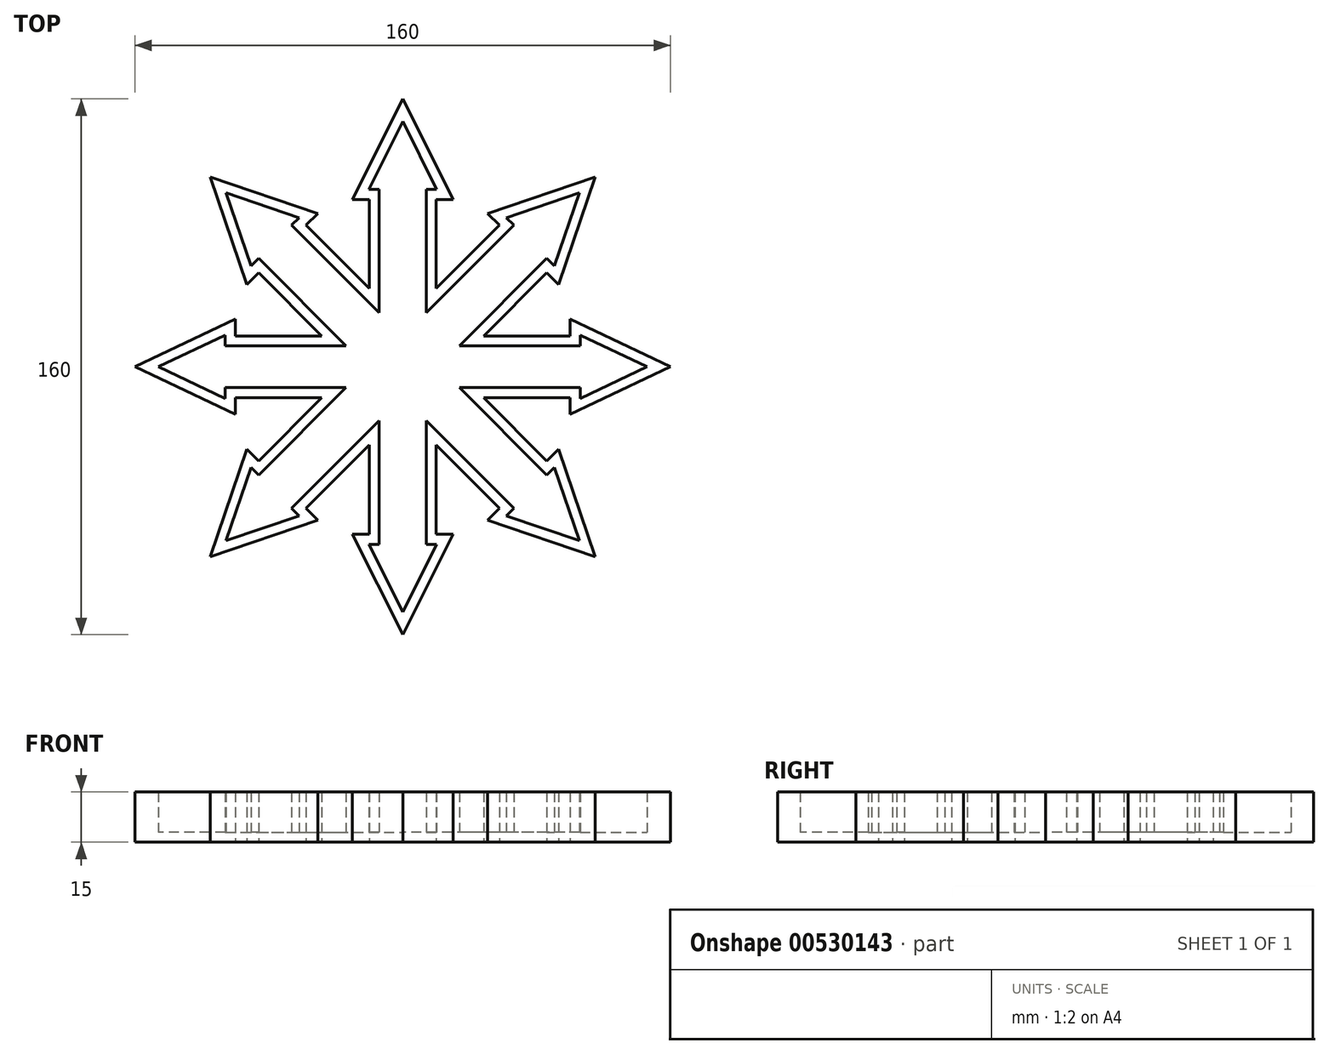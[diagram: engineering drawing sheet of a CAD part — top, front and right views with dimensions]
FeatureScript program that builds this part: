
annotation { "Feature Type Name" : "Feature", "Feature Type Description" : "" }
export const myFeature = defineFeature(function(context is Context, id is Id, definition is map)
    precondition{}
    {
        {
            var Q0;
            Q0=qCreatedBy(makeId("Top.planeOp"),FACE);
            var sketch = newSketch(context, id + "F0", { "sketchPlane" : qUnion([Q0])});
            skPoint(sketch, "E0.middle", {"position": v(0, 0) * mm});
            skPoint(sketch, "E1.endSnap0", {"position": v(-10, 0) * mm});
            skLineSegment(sketch, "E2", {"start": v(-50, 9.21) * mm, "end": v(-10, 9.21) * mm});
            skLineSegment(sketch, "E3", {"start": v(-50, 0) * mm, "end": v(0, 0) * mm});
            skLineSegment(sketch, "E4", {"start": v(-10, 50) * mm, "end": v(-10, 9.21) * mm});
            skLineSegment(sketch, "E5", {"start": v(0, 50) * mm, "end": v(0, 0) * mm});
            skLineSegment(sketch, "E6", {"start": v(-10, 50) * mm, "end": v(-15, 50) * mm});
            skLineSegment(sketch, "E7", {"start": v(-15, 50) * mm, "end": v(0, 80) * mm});
            skLineSegment(sketch, "E8", {"start": v(0, 80) * mm, "end": v(0, 50) * mm});
            skLineSegment(sketch, "E9", {"start": v(-50, 0) * mm, "end": v(-80, 0) * mm});
            skLineSegment(sketch, "E10", {"start": v(-50, 14.21) * mm, "end": v(-80, 0) * mm});
            skLineSegment(sketch, "E11", {"start": v(-43.05, 28.12) * mm, "end": v(-46.59, 24.59) * mm});
            skLineSegment(sketch, "E12", {"start": v(-28.9, 42.26) * mm, "end": v(-25.37, 45.8) * mm});
            skLineSegment(sketch, "E13", {"start": v(-50, 14.21) * mm, "end": v(-50, 9.21) * mm});
            skLineSegment(sketch, "E14", {"start": v(-57.52, 56.74) * mm, "end": v(-46.59, 24.59) * mm});
            skLineSegment(sketch, "E15", {"start": v(-57.52, 56.74) * mm, "end": v(-25.37, 45.8) * mm});
            skLineSegment(sketch, "E16", {"start": v(-10, 9.21) * mm, "end": v(-57.52, 56.74) * mm});
            skLineSegment(sketch, "E17", {"start": v(-28.9, 42.26) * mm, "end": v(-35.98, 35.2) * mm});
            skLineSegment(sketch, "E18", {"start": v(-43.05, 28.12) * mm, "end": v(-35.98, 35.2) * mm});
            skLineSegment(sketch, "E19", {"start": v(-43.05, 28.12) * mm, "end": v(-24.14, 9.21) * mm});
            skLineSegment(sketch, "E20", {"start": v(-28.9, 42.26) * mm, "end": v(-10, 23.36) * mm});
            skLineSegment(sketch, "E21.MirrorCS", {"start": v(28.9, 42.26) * mm, "end": v(25.37, 45.8) * mm});
            skLineSegment(sketch, "E22.MirrorCS", {"start": v(43.05, 28.12) * mm, "end": v(46.59, 24.59) * mm});
            skLineSegment(sketch, "E23.MirrorCS", {"start": v(28.9, 42.26) * mm, "end": v(35.98, 35.2) * mm});
            skLineSegment(sketch, "E24.MirrorCS", {"start": v(43.05, 28.12) * mm, "end": v(35.98, 35.2) * mm});
            skLineSegment(sketch, "E25.MirrorCS", {"start": v(10, 50) * mm, "end": v(15, 50) * mm});
            skLineSegment(sketch, "E26.MirrorCS", {"start": v(50, 14.21) * mm, "end": v(50, 9.21) * mm});
            skLineSegment(sketch, "E27.MirrorCS", {"start": v(10, 9.21) * mm, "end": v(57.52, 56.74) * mm});
            skLineSegment(sketch, "E28.MirrorCS", {"start": v(50, 14.21) * mm, "end": v(80, 0) * mm});
            skLineSegment(sketch, "E29.MirrorCS", {"start": v(50, 0) * mm, "end": v(80, 0) * mm});
            skLineSegment(sketch, "E30.MirrorCS", {"start": v(43.05, 28.12) * mm, "end": v(24.14, 9.21) * mm});
            skLineSegment(sketch, "E31.MirrorCS", {"start": v(57.52, 56.74) * mm, "end": v(25.37, 45.8) * mm});
            skLineSegment(sketch, "E32.MirrorCS", {"start": v(28.9, 42.26) * mm, "end": v(10, 23.36) * mm});
            skLineSegment(sketch, "E33.MirrorCS", {"start": v(15, 50) * mm, "end": v(0, 80) * mm});
            skLineSegment(sketch, "E34.MirrorCS", {"start": v(50, 9.21) * mm, "end": v(10, 9.21) * mm});
            skLineSegment(sketch, "E35.MirrorCS", {"start": v(57.52, 56.74) * mm, "end": v(46.59, 24.59) * mm});
            skPoint(sketch, "E36.MirrorP", {"position": v(10, 0) * mm});
            skLineSegment(sketch, "E37.MirrorCS", {"start": v(10, 50) * mm, "end": v(10, 9.21) * mm});
            skLineSegment(sketch, "E38.MirrorCS", {"start": v(50, 0) * mm, "end": v(0, 0) * mm});
            skLineSegment(sketch, "E39.MirrorCS", {"start": v(-43.05, -28.12) * mm, "end": v(-46.59, -24.59) * mm});
            skLineSegment(sketch, "E40.MirrorCS", {"start": v(-28.9, -42.26) * mm, "end": v(-25.37, -45.8) * mm});
            skLineSegment(sketch, "E41.MirrorCS", {"start": v(28.9, -42.26) * mm, "end": v(25.37, -45.8) * mm});
            skLineSegment(sketch, "E42.MirrorCS", {"start": v(43.05, -28.12) * mm, "end": v(46.59, -24.59) * mm});
            skLineSegment(sketch, "E43.MirrorCS", {"start": v(10, -50) * mm, "end": v(15, -50) * mm});
            skLineSegment(sketch, "E44.MirrorCS", {"start": v(-28.9, -42.26) * mm, "end": v(-35.98, -35.2) * mm});
            skLineSegment(sketch, "E45.MirrorCS", {"start": v(-50, -14.21) * mm, "end": v(-50, -9.21) * mm});
            skLineSegment(sketch, "E46.MirrorCS", {"start": v(43.05, -28.12) * mm, "end": v(35.98, -35.2) * mm});
            skLineSegment(sketch, "E47.MirrorCS", {"start": v(28.9, -42.26) * mm, "end": v(35.98, -35.2) * mm});
            skLineSegment(sketch, "E48.MirrorCS", {"start": v(50, -14.21) * mm, "end": v(50, -9.21) * mm});
            skLineSegment(sketch, "E49.MirrorCS", {"start": v(-10, -50) * mm, "end": v(-15, -50) * mm});
            skLineSegment(sketch, "E50.MirrorCS", {"start": v(-43.05, -28.12) * mm, "end": v(-35.98, -35.2) * mm});
            skLineSegment(sketch, "E51.MirrorCS", {"start": v(0, -50) * mm, "end": v(0, 0) * mm});
            skLineSegment(sketch, "E52.MirrorCS", {"start": v(-28.9, -42.26) * mm, "end": v(-10, -23.36) * mm});
            skLineSegment(sketch, "E53.MirrorCS", {"start": v(57.52, -56.74) * mm, "end": v(46.59, -24.59) * mm});
            skLineSegment(sketch, "E54.MirrorCS", {"start": v(15, -50) * mm, "end": v(0, -80) * mm});
            skLineSegment(sketch, "E55.MirrorCS", {"start": v(10, -9.21) * mm, "end": v(57.52, -56.74) * mm});
            skLineSegment(sketch, "E56.MirrorCS", {"start": v(-57.52, -56.74) * mm, "end": v(-46.59, -24.59) * mm});
            skLineSegment(sketch, "E57.MirrorCS", {"start": v(-10, -50) * mm, "end": v(-10, -9.21) * mm});
            skLineSegment(sketch, "E58.MirrorCS", {"start": v(-15, -50) * mm, "end": v(0, -80) * mm});
            skLineSegment(sketch, "E59.MirrorCS", {"start": v(-50, -14.21) * mm, "end": v(-80, 0) * mm});
            skLineSegment(sketch, "E60.MirrorCS", {"start": v(50, -14.21) * mm, "end": v(80, 0) * mm});
            skLineSegment(sketch, "E61.MirrorCS", {"start": v(57.52, -56.74) * mm, "end": v(25.37, -45.8) * mm});
            skLineSegment(sketch, "E62.MirrorCS", {"start": v(-50, -9.21) * mm, "end": v(-10, -9.21) * mm});
            skLineSegment(sketch, "E63.MirrorCS", {"start": v(-57.52, -56.74) * mm, "end": v(-25.37, -45.8) * mm});
            skLineSegment(sketch, "E64.MirrorCS", {"start": v(28.9, -42.26) * mm, "end": v(10, -23.36) * mm});
            skLineSegment(sketch, "E65.MirrorCS", {"start": v(50, -9.21) * mm, "end": v(10, -9.21) * mm});
            skLineSegment(sketch, "E66.MirrorCS", {"start": v(43.05, -28.12) * mm, "end": v(24.14, -9.21) * mm});
            skLineSegment(sketch, "E67.MirrorCS", {"start": v(-10, -9.21) * mm, "end": v(-57.52, -56.74) * mm});
            skLineSegment(sketch, "E68.MirrorCS", {"start": v(-43.05, -28.12) * mm, "end": v(-24.14, -9.21) * mm});
            skLineSegment(sketch, "E69.MirrorCS", {"start": v(10, -50) * mm, "end": v(10, -9.21) * mm});
            skLineSegment(sketch, "E70.MirrorCS", {"start": v(0, -80) * mm, "end": v(0, -50) * mm});
            skSolve(sketch);
        }
        {
            var Q0;
            Q0 = qSketchRegion(id + "F0", true);
            extrude(context, id + "F1", {"entities" : qUnion([Q0]), "depth" : 10 * mm, "offsetDistance" : 25 * mm});
        }
        {
            var Q0;
            Q0=makeQuery(id+"F1.opExtrude","CAP_FACE",FACE,{"disambiguationData":[OSD([sQuery(id+"F0.wireOp",EDGE,"E22.MirrorCS"),sQuery(id+"F0.wireOp",EDGE,"E21.MirrorCS"),sQuery(id+"F0.wireOp",EDGE,"E25.MirrorCS"),sQuery(id+"F0.wireOp",EDGE,"E11"),sQuery(id+"F0.wireOp",EDGE,"E12"),sQuery(id+"F0.wireOp",EDGE,"E26.MirrorCS"),sQuery(id+"F0.wireOp",EDGE,"E13"),sQuery(id+"F0.wireOp",EDGE,"E6"),sQuery(id+"F0.wireOp",EDGE,"E14"),sQuery(id+"F0.wireOp",EDGE,"E32.MirrorCS"),sQuery(id+"F0.wireOp",EDGE,"E20"),sQuery(id+"F0.wireOp",EDGE,"E2"),sQuery(id+"F0.wireOp",EDGE,"E30.MirrorCS"),sQuery(id+"F0.wireOp",EDGE,"E15"),sQuery(id+"F0.wireOp",EDGE,"E33.MirrorCS"),sQuery(id+"F0.wireOp",EDGE,"E7"),sQuery(id+"F0.wireOp",EDGE,"E10"),sQuery(id+"F0.wireOp",EDGE,"E28.MirrorCS"),sQuery(id+"F0.wireOp",EDGE,"E19"),sQuery(id+"F0.wireOp",EDGE,"E4"),sQuery(id+"F0.wireOp",EDGE,"E31.MirrorCS"),sQuery(id+"F0.wireOp",EDGE,"E34.MirrorCS"),sQuery(id+"F0.wireOp",EDGE,"E37.MirrorCS"),sQuery(id+"F0.wireOp",EDGE,"E35.MirrorCS"),sQuery(id+"F0.wireOp",EDGE,"E39.MirrorCS"),sQuery(id+"F0.wireOp",EDGE,"E40.MirrorCS"),sQuery(id+"F0.wireOp",EDGE,"E42.MirrorCS"),sQuery(id+"F0.wireOp",EDGE,"E41.MirrorCS"),sQuery(id+"F0.wireOp",EDGE,"E48.MirrorCS"),sQuery(id+"F0.wireOp",EDGE,"E43.MirrorCS"),sQuery(id+"F0.wireOp",EDGE,"E45.MirrorCS"),sQuery(id+"F0.wireOp",EDGE,"E49.MirrorCS"),sQuery(id+"F0.wireOp",EDGE,"E53.MirrorCS"),sQuery(id+"F0.wireOp",EDGE,"E52.MirrorCS"),sQuery(id+"F0.wireOp",EDGE,"E57.MirrorCS"),sQuery(id+"F0.wireOp",EDGE,"E54.MirrorCS"),sQuery(id+"F0.wireOp",EDGE,"E65.MirrorCS"),sQuery(id+"F0.wireOp",EDGE,"E64.MirrorCS"),sQuery(id+"F0.wireOp",EDGE,"E68.MirrorCS"),sQuery(id+"F0.wireOp",EDGE,"E56.MirrorCS"),sQuery(id+"F0.wireOp",EDGE,"E63.MirrorCS"),sQuery(id+"F0.wireOp",EDGE,"E59.MirrorCS"),sQuery(id+"F0.wireOp",EDGE,"E58.MirrorCS"),sQuery(id+"F0.wireOp",EDGE,"E62.MirrorCS"),sQuery(id+"F0.wireOp",EDGE,"E61.MirrorCS"),sQuery(id+"F0.wireOp",EDGE,"E69.MirrorCS"),sQuery(id+"F0.wireOp",EDGE,"E60.MirrorCS"),sQuery(id+"F0.wireOp",EDGE,"E66.MirrorCS")])],"isStart":false});
            extrude(context, id + "F2", {"entities" : qUnion([Q0]), "operationType" : NewBodyOperationType.ADD, "depth" : 5 * mm, "offsetDistance" : 25 * mm});
        }
        {
            var Q0;
            Q0=makeQuery(id+"F2.opExtrude","CAP_FACE",FACE,{"disambiguationData":[OSD([sQuery(id+"F0.wireOp",EDGE,"E22.MirrorCS"),sQuery(id+"F0.wireOp",EDGE,"E21.MirrorCS"),sQuery(id+"F0.wireOp",EDGE,"E25.MirrorCS"),sQuery(id+"F0.wireOp",EDGE,"E11"),sQuery(id+"F0.wireOp",EDGE,"E12"),sQuery(id+"F0.wireOp",EDGE,"E26.MirrorCS"),sQuery(id+"F0.wireOp",EDGE,"E13"),sQuery(id+"F0.wireOp",EDGE,"E6"),sQuery(id+"F0.wireOp",EDGE,"E14"),sQuery(id+"F0.wireOp",EDGE,"E32.MirrorCS"),sQuery(id+"F0.wireOp",EDGE,"E20"),sQuery(id+"F0.wireOp",EDGE,"E2"),sQuery(id+"F0.wireOp",EDGE,"E30.MirrorCS"),sQuery(id+"F0.wireOp",EDGE,"E15"),sQuery(id+"F0.wireOp",EDGE,"E33.MirrorCS"),sQuery(id+"F0.wireOp",EDGE,"E7"),sQuery(id+"F0.wireOp",EDGE,"E10"),sQuery(id+"F0.wireOp",EDGE,"E28.MirrorCS"),sQuery(id+"F0.wireOp",EDGE,"E19"),sQuery(id+"F0.wireOp",EDGE,"E4"),sQuery(id+"F0.wireOp",EDGE,"E31.MirrorCS"),sQuery(id+"F0.wireOp",EDGE,"E34.MirrorCS"),sQuery(id+"F0.wireOp",EDGE,"E37.MirrorCS"),sQuery(id+"F0.wireOp",EDGE,"E35.MirrorCS"),sQuery(id+"F0.wireOp",EDGE,"E39.MirrorCS"),sQuery(id+"F0.wireOp",EDGE,"E40.MirrorCS"),sQuery(id+"F0.wireOp",EDGE,"E42.MirrorCS"),sQuery(id+"F0.wireOp",EDGE,"E41.MirrorCS"),sQuery(id+"F0.wireOp",EDGE,"E48.MirrorCS"),sQuery(id+"F0.wireOp",EDGE,"E43.MirrorCS"),sQuery(id+"F0.wireOp",EDGE,"E45.MirrorCS"),sQuery(id+"F0.wireOp",EDGE,"E49.MirrorCS"),sQuery(id+"F0.wireOp",EDGE,"E53.MirrorCS"),sQuery(id+"F0.wireOp",EDGE,"E52.MirrorCS"),sQuery(id+"F0.wireOp",EDGE,"E57.MirrorCS"),sQuery(id+"F0.wireOp",EDGE,"E54.MirrorCS"),sQuery(id+"F0.wireOp",EDGE,"E65.MirrorCS"),sQuery(id+"F0.wireOp",EDGE,"E64.MirrorCS"),sQuery(id+"F0.wireOp",EDGE,"E68.MirrorCS"),sQuery(id+"F0.wireOp",EDGE,"E56.MirrorCS"),sQuery(id+"F0.wireOp",EDGE,"E63.MirrorCS"),sQuery(id+"F0.wireOp",EDGE,"E59.MirrorCS"),sQuery(id+"F0.wireOp",EDGE,"E58.MirrorCS"),sQuery(id+"F0.wireOp",EDGE,"E62.MirrorCS"),sQuery(id+"F0.wireOp",EDGE,"E61.MirrorCS"),sQuery(id+"F0.wireOp",EDGE,"E69.MirrorCS"),sQuery(id+"F0.wireOp",EDGE,"E60.MirrorCS"),sQuery(id+"F0.wireOp",EDGE,"E66.MirrorCS")])],"isStart":false});
            shell(context, id + "F3", {"entities" : qUnion([Q0]), "thickness" : 3 * mm});
        }
    });
